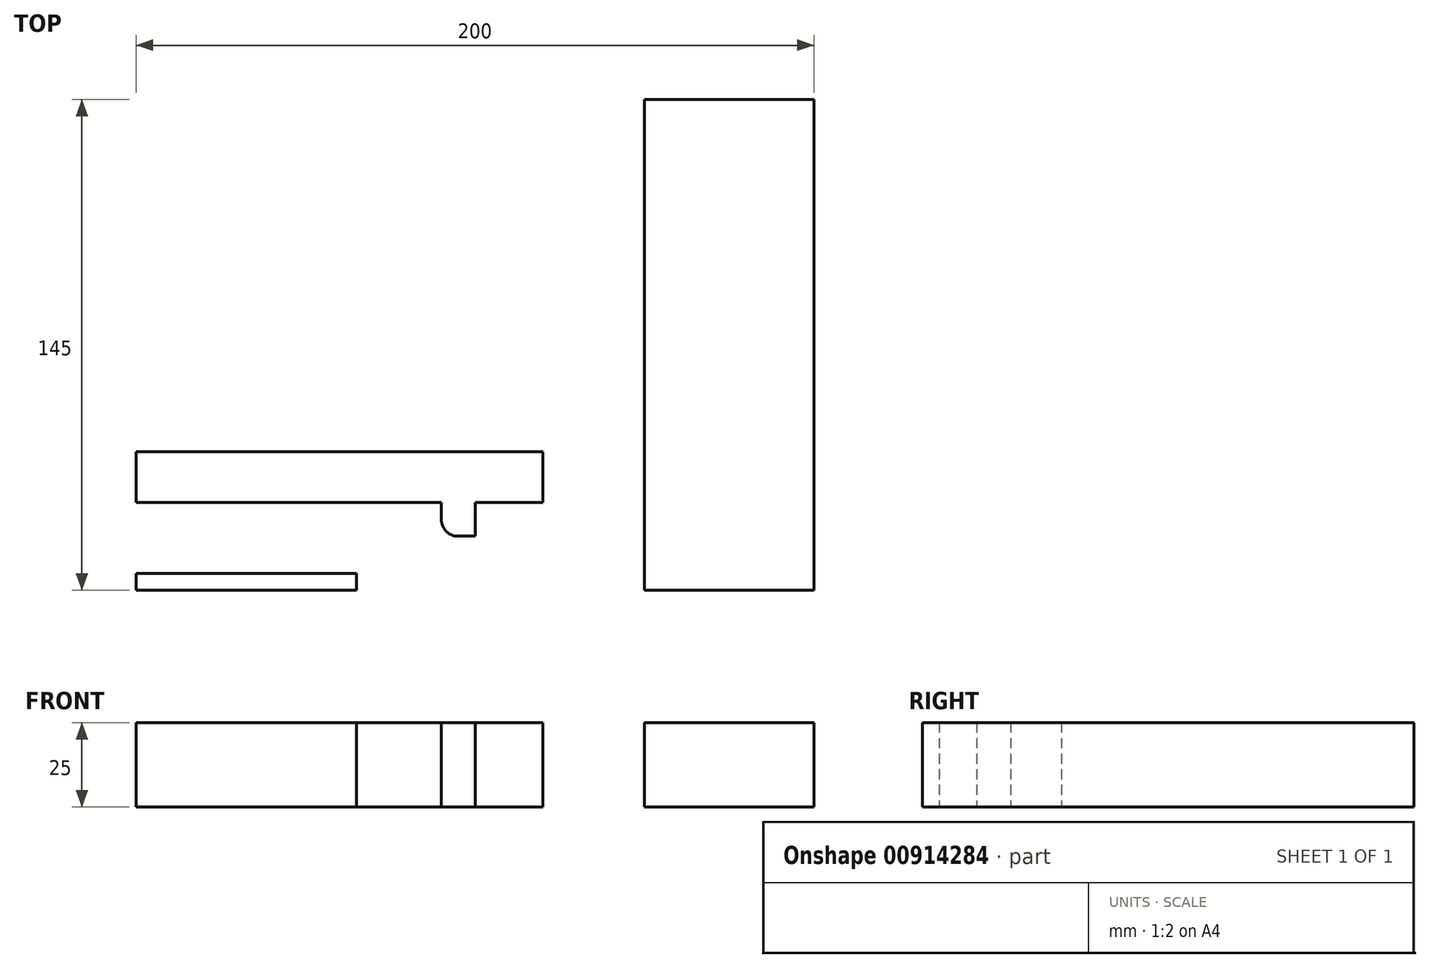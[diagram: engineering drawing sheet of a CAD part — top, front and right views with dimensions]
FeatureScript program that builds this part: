
annotation { "Feature Type Name" : "Feature", "Feature Type Description" : "" }
export const myFeature = defineFeature(function(context is Context, id is Id, definition is map)
    precondition{}
    {
        {
            var Q0;
            Q0=qCreatedBy(makeId("Top.planeOp"),FACE);
            var sketch = newSketch(context, id + "F0", { "sketchPlane" : qUnion([Q0])});
            skLineSegment(sketch, "E0.bottom", {"start": v(174.07, -90.93) * mm, "end": v(374.07, -90.93) * mm});
            skLineSegment(sketch, "E0.top", {"start": v(174.07, -235.93) * mm, "end": v(374.07, -235.93) * mm});
            skLineSegment(sketch, "E0.left", {"start": v(174.07, -90.93) * mm, "end": v(174.07, -235.93) * mm});
            skLineSegment(sketch, "E0.right", {"start": v(374.07, -90.93) * mm, "end": v(374.07, -235.93) * mm});
            skLineSegment(sketch, "E1.bottom", {"start": v(174.07, -90.93) * mm, "end": v(324.07, -90.93) * mm});
            skLineSegment(sketch, "E1.top", {"start": v(174.07, -180.93) * mm, "end": v(324.07, -180.93) * mm});
            skLineSegment(sketch, "E1.left", {"start": v(174.07, -90.93) * mm, "end": v(174.07, -180.93) * mm});
            skLineSegment(sketch, "E1.right", {"start": v(324.07, -90.93) * mm, "end": v(324.07, -180.93) * mm});
            skLineSegment(sketch, "E2.bottom", {"start": v(374.07, -90.93) * mm, "end": v(354.07, -90.93) * mm});
            skLineSegment(sketch, "E2.top", {"start": v(374.07, -135.93) * mm, "end": v(354.07, -135.93) * mm});
            skLineSegment(sketch, "E2.left", {"start": v(374.07, -90.93) * mm, "end": v(374.07, -135.93) * mm});
            skLineSegment(sketch, "E2.right", {"start": v(354.07, -90.93) * mm, "end": v(354.07, -135.93) * mm});
            skLineSegment(sketch, "E3.bottom", {"start": v(354.07, -90.93) * mm, "end": v(334.07, -90.93) * mm});
            skLineSegment(sketch, "E3.top", {"start": v(354.07, -135.93) * mm, "end": v(334.07, -135.93) * mm});
            skLineSegment(sketch, "E3.right", {"start": v(334.07, -90.93) * mm, "end": v(334.07, -135.93) * mm});
            skLineSegment(sketch, "E4.bottom", {"start": v(174.07, -180.93) * mm, "end": v(280.07, -180.93) * mm});
            skLineSegment(sketch, "E4.top", {"start": v(174.07, -194.93) * mm, "end": v(280.07, -194.93) * mm});
            skLineSegment(sketch, "E4.left", {"start": v(174.07, -180.93) * mm, "end": v(174.07, -194.93) * mm});
            skLineSegment(sketch, "E4.right", {"start": v(280.07, -180.93) * mm, "end": v(280.07, -194.93) * mm});
            skLineSegment(sketch, "E5.bottom", {"start": v(174.07, -194.93) * mm, "end": v(294.07, -194.93) * mm});
            skLineSegment(sketch, "E5.top", {"start": v(174.07, -209.93) * mm, "end": v(294.07, -209.93) * mm});
            skLineSegment(sketch, "E5.left", {"start": v(174.07, -194.93) * mm, "end": v(174.07, -209.93) * mm});
            skLineSegment(sketch, "E5.right", {"start": v(294.07, -194.93) * mm, "end": v(294.07, -209.93) * mm});
            skLineSegment(sketch, "E6.bottom", {"start": v(280.07, -180.93) * mm, "end": v(315.07, -180.93) * mm});
            skLineSegment(sketch, "E6.top", {"start": v(280.07, -190.93) * mm, "end": v(315.07, -190.93) * mm});
            skLineSegment(sketch, "E6.left", {"start": v(280.07, -180.93) * mm, "end": v(280.07, -190.93) * mm});
            skLineSegment(sketch, "E6.right", {"start": v(315.07, -180.93) * mm, "end": v(315.07, -190.93) * mm});
            skLineSegment(sketch, "E7.bottom", {"start": v(374.07, -135.93) * mm, "end": v(324.07, -135.93) * mm});
            skLineSegment(sketch, "E7.top", {"start": v(374.07, -165.93) * mm, "end": v(324.07, -165.93) * mm});
            skLineSegment(sketch, "E7.left", {"start": v(374.07, -135.93) * mm, "end": v(374.07, -165.93) * mm});
            skLineSegment(sketch, "E7.right", {"start": v(324.07, -135.93) * mm, "end": v(324.07, -165.93) * mm});
            skLineSegment(sketch, "E8.left", {"start": v(294.07, -194.93) * mm, "end": v(294.07, -199.93) * mm});
            skLineSegment(sketch, "E9.bottom", {"start": v(174.07, -209.93) * mm, "end": v(264.07, -209.93) * mm});
            skLineSegment(sketch, "E9.top", {"start": v(174.07, -216.93) * mm, "end": v(264.07, -216.93) * mm});
            skLineSegment(sketch, "E9.left", {"start": v(174.07, -209.93) * mm, "end": v(174.07, -216.93) * mm});
            skLineSegment(sketch, "E9.right", {"start": v(264.07, -209.93) * mm, "end": v(264.07, -216.93) * mm});
            skLineSegment(sketch, "E10.bottom", {"start": v(264.07, -216.93) * mm, "end": v(174.07, -216.93) * mm});
            skLineSegment(sketch, "E10.top", {"start": v(264.07, -223.93) * mm, "end": v(174.07, -223.93) * mm});
            skLineSegment(sketch, "E10.left", {"start": v(264.07, -216.93) * mm, "end": v(264.07, -223.93) * mm});
            skLineSegment(sketch, "E10.right", {"start": v(174.07, -216.93) * mm, "end": v(174.07, -223.93) * mm});
            skLineSegment(sketch, "E11.bottom", {"start": v(174.07, -223.93) * mm, "end": v(264.07, -223.93) * mm});
            skLineSegment(sketch, "E11.top", {"start": v(174.07, -230.93) * mm, "end": v(264.07, -230.93) * mm});
            skLineSegment(sketch, "E11.left", {"start": v(174.07, -223.93) * mm, "end": v(174.07, -230.93) * mm});
            skLineSegment(sketch, "E11.right", {"start": v(264.07, -223.93) * mm, "end": v(264.07, -230.93) * mm});
            skLineSegment(sketch, "E12.bottom", {"start": v(374.07, -235.93) * mm, "end": v(324.07, -235.93) * mm});
            skLineSegment(sketch, "E12.top", {"start": v(374.07, -180.93) * mm, "end": v(324.07, -180.93) * mm});
            skLineSegment(sketch, "E12.left", {"start": v(374.07, -235.93) * mm, "end": v(374.07, -180.93) * mm});
            skLineSegment(sketch, "E12.right", {"start": v(324.07, -235.93) * mm, "end": v(324.07, -180.93) * mm});
            skLineSegment(sketch, "E13.bottom", {"start": v(174.07, -230.93) * mm, "end": v(239.07, -230.93) * mm});
            skLineSegment(sketch, "E13.top", {"start": v(174.07, -235.93) * mm, "end": v(239.07, -235.93) * mm});
            skLineSegment(sketch, "E13.left", {"start": v(174.07, -230.93) * mm, "end": v(174.07, -235.93) * mm});
            skLineSegment(sketch, "E13.right", {"start": v(239.07, -230.93) * mm, "end": v(239.07, -235.93) * mm});
            skLineSegment(sketch, "E14.bottom", {"start": v(264.07, -209.93) * mm, "end": v(274.07, -209.93) * mm});
            skLineSegment(sketch, "E14.top", {"start": v(264.07, -219.93) * mm, "end": v(274.07, -219.93) * mm});
            skLineSegment(sketch, "E14.left", {"start": v(264.07, -209.93) * mm, "end": v(264.07, -219.93) * mm});
            skLineSegment(sketch, "E14.right", {"start": v(274.07, -209.93) * mm, "end": v(274.07, -219.93) * mm});
            skCircle(sketch, "E15", {"center": v(269.07, -214.93) * mm, "radius": 5 * mm});
            skLineSegment(sketch, "E16.bottom", {"start": v(274.07, -209.93) * mm, "end": v(284.07, -209.93) * mm});
            skLineSegment(sketch, "E16.left", {"start": v(274.07, -209.93) * mm, "end": v(274.07, -217.93) * mm});
            skLineSegment(sketch, "E17.left", {"start": v(264.07, -219.93) * mm, "end": v(264.07, -224.93) * mm});
            skSolve(sketch);
        }
        {
            var Q0;
            {var subQ1=sQuery(id+"F0.wireOp",EDGE,"E1.bottom");Q0=makeQuery(id+"F0.imprint","IMPRINT",FACE,{"disambiguationData":[TD([[makeQuery(id+"F0.imprint","IMPRINT",EDGE,{"derivedFrom":subQ1}),-1.0]])]});}
            var Q1;
            Q1=makeQuery(id+"F0.imprint","IMPRINT",FACE,{"disambiguationData":[TD([[makeQuery(id+"F0.imprint","IMPRINT",EDGE,{"derivedFrom":sQuery(id+"F0.wireOp",EDGE,"E2.bottom")}),1.0]])]});
            var Q2;
            Q2=makeQuery(id+"F0.imprint","IMPRINT",FACE,{"disambiguationData":[TD([[makeQuery(id+"F0.imprint","IMPRINT",EDGE,{"derivedFrom":sQuery(id+"F0.wireOp",EDGE,"E6.bottom")}),-1.0]])]});
            var Q3;
            Q3=makeQuery(id+"F0.imprint","IMPRINT",FACE,{"disambiguationData":[TD([[makeQuery(id+"F0.imprint","IMPRINT",EDGE,{"derivedFrom":sQuery(id+"F0.wireOp",EDGE,"E0.right")}),-1.0]])]});
            var Q4;
            Q4=makeQuery(id+"F0.imprint","IMPRINT",FACE,{"disambiguationData":[TD([[makeQuery(id+"F0.imprint","IMPRINT",EDGE,{"derivedFrom":sQuery(id+"F0.wireOp",EDGE,"E4.bottom")}),-1.0]])]});
            var Q5;
            Q5=makeQuery(id+"F0.imprint","IMPRINT",FACE,{"disambiguationData":[TD([[makeQuery(id+"F0.imprint","IMPRINT",EDGE,{"derivedFrom":sQuery(id+"F0.wireOp",EDGE,"E12.bottom")}),-1.0]])]});
            var Q6;
            Q6=makeQuery(id+"F0.imprint","IMPRINT",FACE,{"disambiguationData":[TD([[makeQuery(id+"F0.imprint","IMPRINT",EDGE,{"derivedFrom":sQuery(id+"F0.wireOp",EDGE,"E0.top")}),1.0]])]});
            var Q7;
            Q7=makeQuery(id+"F0.imprint","IMPRINT",FACE,{"disambiguationData":[TD([[makeQuery(id+"F0.imprint","IMPRINT",EDGE,{"derivedFrom":sQuery(id+"F0.wireOp",EDGE,"E5.top")}),1.0]])]});
            var Q8;
            {var subQ1=sQuery(id+"F0.wireOp",EDGE,"E11.bottom");Q8=makeQuery(id+"F0.imprint","IMPRINT",FACE,{"disambiguationData":[TD([[makeQuery(id+"F0.imprint","IMPRINT",EDGE,{"derivedFrom":subQ1}),-1.0]])]});}
            var Q9;
            Q9=makeQuery(id+"F0.imprint","IMPRINT",FACE,{"disambiguationData":[TD([[makeQuery(id+"F0.imprint","IMPRINT",EDGE,{"derivedFrom":sQuery(id+"F0.wireOp",EDGE,"E3.bottom")}),1.0]])]});
            var Q10;
            {var subQ0=sQuery(id+"F0.wireOp",EDGE,"E0.bottom");Q10=makeQuery(id+"F0.imprint","IMPRINT",FACE,{"disambiguationData":[TD([[makeQuery(id+"F0.imprint","IMPRINT",EDGE,{"derivedFrom":subQ0}),-1.0]])]});}
            var Q11;
            Q11=makeQuery(id+"F0.imprint","IMPRINT",FACE,{"disambiguationData":[TD([[makeQuery(id+"F0.imprint","IMPRINT",EDGE,{"derivedFrom":sQuery(id+"F0.wireOp",EDGE,"E13.bottom")}),-1.0]])]});
            var Q12;
            {var subQ2=sQuery(id+"F0.wireOp",EDGE,"E9.bottom");Q12=makeQuery(id+"F0.imprint","IMPRINT",FACE,{"disambiguationData":[TD([[makeQuery(id+"F0.imprint","IMPRINT",EDGE,{"derivedFrom":subQ2}),-1.0]])]});}
            var Q13;
            Q13=makeQuery(id+"F0.imprint","IMPRINT",FACE,{"disambiguationData":[TD([[makeQuery(id+"F0.imprint","IMPRINT",EDGE,{"derivedFrom":sQuery(id+"F0.wireOp",EDGE,"E7.top")}),-1.0]])]});
            var Q14;
            {var subQ2=sQuery(id+"F0.wireOp",EDGE,"E10.bottom");Q14=makeQuery(id+"F0.imprint","IMPRINT",FACE,{"disambiguationData":[TD([[makeQuery(id+"F0.imprint","IMPRINT",EDGE,{"derivedFrom":subQ2}),1.0]])]});}
            var Q15;
            {var subQ1=sQuery(id+"F0.wireOp",EDGE,"E14.bottom");var subQ3=sQuery(id+"F0.wireOp",EDGE,"E15");var subQ4=makeQuery(id+"F0.imprint","INTERSECT",VERTEX,{"derivedFrom":[subQ1,subQ3]});Q15=makeQuery(id+"F0.imprint","IMPRINT",FACE,{"disambiguationData":[TD([[makeQuery(id+"F0.imprint","IMPRINT",EDGE,{"disambiguationData":[TD([[subQ4,-1.0]])],"derivedFrom":subQ3}),-1.0]])]});}
            var Q16;
            {var subQ0=sQuery(id+"F0.wireOp",EDGE,"E15");var subQ1=makeQuery(id+"F0.imprint","INTERSECT",VERTEX,{"derivedFrom":[sQuery(id+"F0.wireOp",EDGE,"E14.bottom"),subQ0]});Q16=makeQuery(id+"F0.imprint","IMPRINT",FACE,{"disambiguationData":[TD([[makeQuery(id+"F0.imprint","IMPRINT",EDGE,{"disambiguationData":[TD([[subQ1,1.0]])],"derivedFrom":subQ0}),1.0]])]});}
            var Q17;
            {var subQ0=sQuery(id+"F0.wireOp",EDGE,"E14.right");Q17=makeQuery(id+"F0.imprint","IMPRINT",FACE,{"disambiguationData":[TD([[makeQuery(id+"F0.imprint","IMPRINT",EDGE,{"derivedFrom":subQ0}),-1.0]])]});}
            var Q18;
            {var subQ1=sQuery(id+"F0.wireOp",EDGE,"E14.bottom");var subQ3=sQuery(id+"F0.wireOp",EDGE,"E15");var subQ4=makeQuery(id+"F0.imprint","INTERSECT",VERTEX,{"derivedFrom":[subQ1,subQ3]});Q18=makeQuery(id+"F0.imprint","IMPRINT",FACE,{"disambiguationData":[TD([[makeQuery(id+"F0.imprint","IMPRINT",EDGE,{"disambiguationData":[TD([[subQ4,1.0]])],"derivedFrom":subQ3}),-1.0]])]});}
            var Q19;
            {var subQ0=sQuery(id+"F0.wireOp",EDGE,"E14.left");var subQ5=makeQuery(id+"F0.imprint","INTERSECT",VERTEX,{"derivedFrom":[sQuery(id+"F0.wireOp",EDGE,"E10.bottom"),subQ0]});Q19=makeQuery(id+"F0.imprint","IMPRINT",FACE,{"disambiguationData":[TD([[makeQuery(id+"F0.imprint","IMPRINT",EDGE,{"disambiguationData":[TD([[subQ5,1.0]])],"derivedFrom":subQ0}),1.0]])]});}
            extrude(context, id + "F1", {"entities" : qUnion([Q0, Q1, Q2, Q3, Q4, Q5, Q6, Q7, Q8, Q9, Q10, Q11, Q12, Q13, Q14, Q15, Q16, Q17, Q18, Q19]), "depth" : 25 * mm, "offsetDistance" : 25 * mm});
        }
    });
